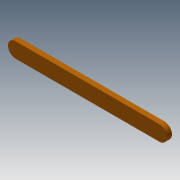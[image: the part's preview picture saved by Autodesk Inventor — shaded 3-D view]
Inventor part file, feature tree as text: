
AUTODESK INVENTOR PART (.ipt)
format: ipt  version: 2013 (Build 170138000, 138)  size: 202,752 bytes
history: native  units: mm
features: sketch x15, extrude x14
ambient origin geometry x8: Origin, YZ Plane, XZ Plane, XY Plane, X Axis, Y Axis, Z Axis, Center Point
bodies: Solid1 (feature_tree)
feature tree (29):
  sketch  "Sketch1"  dims[d6=57.0mm d7=6.0mm]
  extrude  "Extrusion1"  Depth=6.0mm
  extrude  "Extrusion2"  Depth=10.0mm
  extrude  "Extrusion3"  Depth=8.0mm
  extrude  "Extrusion4"  Depth=1.0mm TaperAngle=0.0deg
  extrude  "Extrusion5"  Depth=3.0mm
  sketch  "Sketch7"  dims[d24=2.0mm d25=0.0mm d26=7.0mm d27=0.0mm]
  extrude  "Extrusion6"  Depth=2.0mm TaperAngle=0.0deg
  extrude  "Extrusion7"  Depth=7.0mm TaperAngle=0.0deg
  extrude  "Extrusion8"  Depth=8.0mm
  extrude  "Extrusion9"  Depth=7.0mm
  extrude  "Extrusion10"  Depth=0.01mm
  sketch  "Sketch12"  dims[d39=6.0mm d40=0.01mm]
  extrude  "Extrusion11"  Depth=0.01mm
  extrude  "Extrusion12"  Depth=0.01mm
  extrude  "Extrusion13"  Depth=0.01mm
  extrude  "Extrusion14"  Depth=2.0mm TaperAngle=0.0deg
  sketch  "Sketch2"  dims[d8=2.0mm d9=0.0mm d10=10.0mm]
  sketch  "Sketch3"  dims[d11=7.0mm d12=0.0mm d13=8.0mm]
  sketch  "Sketch4"  dims[d14=7.0mm d15=0.0mm d16=1.0mm d17=0.0mm]
  sketch  "Sketch5"  dims[d18=1.0mm d19=0.0mm d20=3.0mm]
  sketch  "Sketch6"  dims[d21=3.0mm d22=2.0mm d23=0.0mm]
  sketch  "Sketch8"  dims[d28=8.0mm d29=0.0mm d32=8.0mm]
  sketch  "Sketch9"  dims[d33=7.0mm d34=7.0mm]
  sketch  "Sketch10"  dims[d35=17.5mm d36=0.01mm]
  sketch  "Sketch11"  dims[d37=6.0mm d38=0.01mm]
  sketch  "Sketch13"  dims[d41=6.0mm d42=0.01mm]
  sketch  "Sketch14"  dims[d43=6.0mm d44=2.0mm d45=0.0mm]
  sketch  "Sketch15"  dims[d46=0.01mm d47=0.01mm d48=2.0mm d49=0.0mm d50=2.0mm d51=0.0mm d52=0.1mm d53=2.0mm d54=0.0mm d55=0.1mm d56=2.0mm d57=0.0mm]
